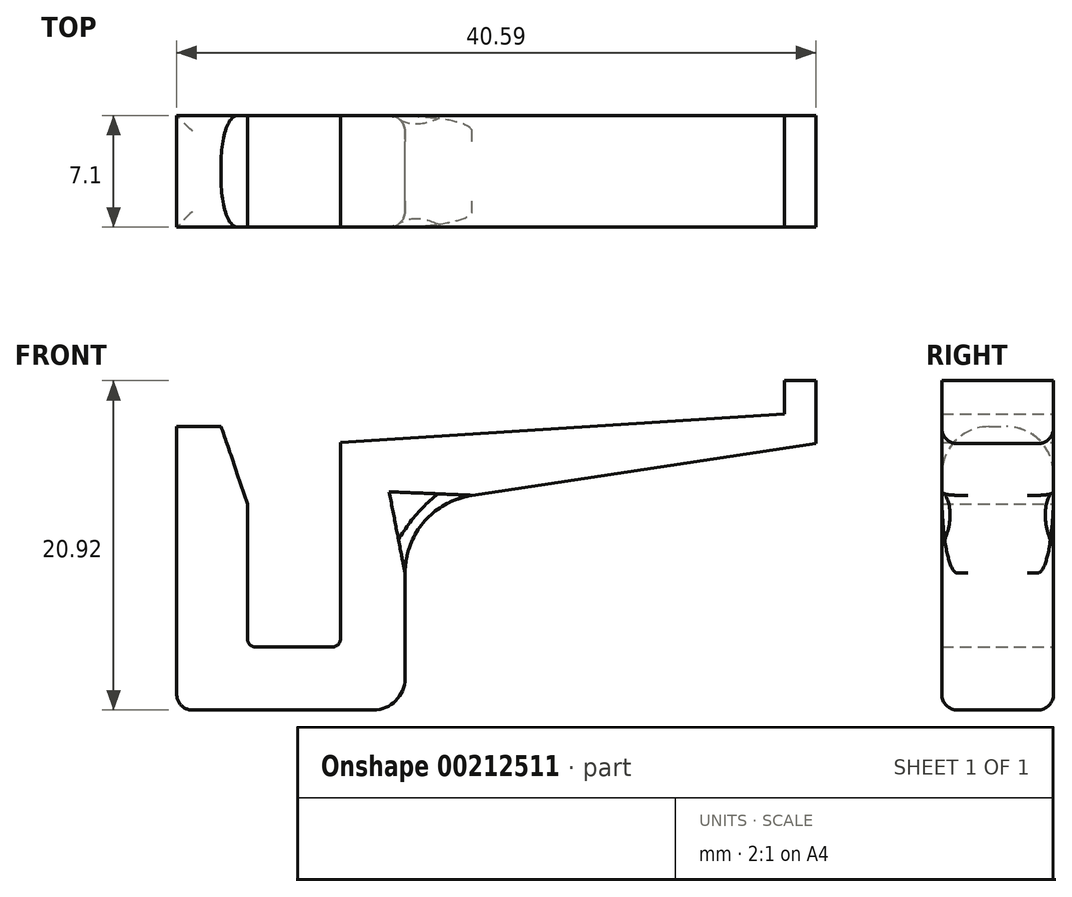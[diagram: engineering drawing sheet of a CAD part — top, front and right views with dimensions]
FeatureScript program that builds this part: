
annotation { "Feature Type Name" : "Feature", "Feature Type Description" : "" }
export const myFeature = defineFeature(function(context is Context, id is Id, definition is map)
    precondition{}
    {
        {
            var Q0;
            Q0=qCreatedBy(makeId("Front.planeOp"),FACE);
            var sketch = newSketch(context, id + "F0", { "sketchPlane" : qUnion([Q0])});
            skLineSegment(sketch, "E0", {"start": v(4.69, 3.9) * mm, "end": v(4.69, 12.98) * mm});
            skLineSegment(sketch, "E1", {"start": v(0.19, 12.9) * mm, "end": v(0.19, -0.1) * mm});
            skLineSegment(sketch, "E2", {"start": v(0.19, -0.1) * mm, "end": v(14.69, -0.1) * mm});
            skLineSegment(sketch, "E3", {"start": v(14.69, -0.1) * mm, "end": v(14.69, 8.9) * mm});
            skLineSegment(sketch, "E4", {"start": v(10.59, 12.9) * mm, "end": v(10.59, 3.9) * mm});
            skLineSegment(sketch, "E5", {"start": v(10.59, 3.9) * mm, "end": v(4.69, 3.9) * mm});
            skLineSegment(sketch, "E6", {"start": v(1.34, 17.9) * mm, "end": v(3.01, 17.9) * mm});
            skLineSegment(sketch, "E7", {"start": v(0.19, 12.9) * mm, "end": v(0.19, 17.9) * mm});
            skLineSegment(sketch, "E8", {"start": v(1.34, 17.9) * mm, "end": v(0.19, 17.9) * mm});
            skLineSegment(sketch, "E9", {"start": v(10.59, 12.9) * mm, "end": v(10.59, 16.9) * mm});
            skLineSegment(sketch, "E10", {"start": v(10.59, 16.9) * mm, "end": v(38.78, 18.7) * mm});
            skLineSegment(sketch, "E11", {"start": v(40.78, 18.82) * mm, "end": v(40.78, 16.82) * mm});
            skLineSegment(sketch, "E12", {"start": v(14.69, 8.9) * mm, "end": v(14.69, 12.9) * mm});
            skLineSegment(sketch, "E13", {"start": v(40.78, 16.82) * mm, "end": v(14.69, 12.9) * mm});
            skLineSegment(sketch, "E14", {"start": v(40.78, 18.82) * mm, "end": v(40.78, 20.82) * mm});
            skLineSegment(sketch, "E15", {"start": v(40.78, 20.82) * mm, "end": v(38.78, 20.82) * mm});
            skLineSegment(sketch, "E16", {"start": v(38.78, 20.82) * mm, "end": v(38.78, 18.7) * mm});
            skLineSegment(sketch, "E17", {"start": v(3.01, 17.9) * mm, "end": v(4.69, 12.98) * mm});
            skPoint(sketch, "E18.orphan", {"position": v(4.69, 17.9) * mm});
            skSolve(sketch);
        }
        {
            var Q0;
            Q0=makeQuery(id+"F0.imprint","IMPRINT",FACE,{"disambiguationData":[TD([[makeQuery(id+"F0.imprint","IMPRINT",EDGE,{"derivedFrom":sQuery(id+"F0.wireOp",EDGE,"E0")}),1.0]])]});
            extrude(context, id + "F1", {"entities" : qUnion([Q0]), "endBound" : BoundingType.SYMMETRIC, "depth" : 7.1 * mm});
        }
        {
            var Q0;
            Q0=makeQuery(id+"F1.opExtrude","CAP_EDGE",EDGE,{"disambiguationData":[OSD([sQuery(id+"F0.wireOp",EDGE,"FIeobUB5-AtsX-6hmR-oWOE-ariMEtalVAF4")])],"isStart":false});
            var Q1;
            Q1=makeQuery(id+"F1.opExtrude","SWEPT_EDGE",EDGE,{"disambiguationData":[OSD([sQuery(id+"F0.wireOp",EDGE,"5An7Op3Y-UuDj-N7TT-U8in-DWvZWZOJ67oY"),sQuery(id+"F0.wireOp",EDGE,"FIeobUB5-AtsX-6hmR-oWOE-ariMEtalVAF4")])]});
            var Q2;
            Q2=makeQuery(id+"F1.opExtrude","CAP_EDGE",EDGE,{"disambiguationData":[OSD([sQuery(id+"F0.wireOp",EDGE,"FIeobUB5-AtsX-6hmR-oWOE-ariMEtalVAF4")])],"isStart":true});
            var Q3;
            Q3=makeQuery(id+"F1.opExtrude","SWEPT_EDGE",EDGE,{"disambiguationData":[OSD([sQuery(id+"F0.wireOp",EDGE,"5An7Op3Y-UuDj-N7TT-U8in-DWvZWZOJ67oY"),sQuery(id+"F0.wireOp",EDGE,"z2avqr7E-bqeD-pCF3-mnLU-iVtxecrn7GOb")])]});
            var Q4;
            Q4=makeQuery(id+"F1.opExtrude","CAP_EDGE",EDGE,{"disambiguationData":[OSD([sQuery(id+"F0.wireOp",EDGE,"z2avqr7E-bqeD-pCF3-mnLU-iVtxecrn7GOb")])],"isStart":false});
            var Q5;
            Q5=makeQuery(id+"F1.opExtrude","CAP_EDGE",EDGE,{"disambiguationData":[OSD([sQuery(id+"F0.wireOp",EDGE,"z2avqr7E-bqeD-pCF3-mnLU-iVtxecrn7GOb")])],"isStart":true});
            var Q6;
            Q6=makeQuery(id+"F1.opExtrude","SWEPT_EDGE",EDGE,{"disambiguationData":[OSD([sQuery(id+"F0.wireOp",EDGE,"E0"),sQuery(id+"F0.wireOp",EDGE,"E5")])]});
            var Q7;
            Q7=makeQuery(id+"F1.opExtrude","SWEPT_EDGE",EDGE,{"disambiguationData":[OSD([sQuery(id+"F0.wireOp",EDGE,"E4"),sQuery(id+"F0.wireOp",EDGE,"E5")])]});
            fillet(context, id + "F2", {"entities" : qUnion([Q0, Q1, Q2, Q3, Q4, Q5, Q6, Q7]), "radius" : 0.5 * mm, "tangentPropagation" : true, "allowEdgeOverflow" : false});
        }
        {
            var Q0;
            Q0=makeQuery(id+"F1.opExtrude","SWEPT_EDGE",EDGE,{"disambiguationData":[OSD([sQuery(id+"F0.wireOp",EDGE,"E3"),sQuery(id+"F0.wireOp",EDGE,"z2avqr7E-bqeD-pCF3-mnLU-iVtxecrn7GOb")])]});
            fillet(context, id + "F3", {"entities" : qUnion([Q0]), "radius" : 2 * mm, "tangentPropagation" : true, "allowEdgeOverflow" : false});
        }
        {
            var Q0;
            Q0=makeQuery(id+"F1.opExtrude","SWEPT_EDGE",EDGE,{"disambiguationData":[OSD([sQuery(id+"F0.wireOp",EDGE,"FIeobUB5-AtsX-6hmR-oWOE-ariMEtalVAF4"),sQuery(id+"F0.wireOp",EDGE,"E4")])]});
            var Q1;
            Q1=makeQuery(id+"F1.opExtrude","CAP_EDGE",EDGE,{"disambiguationData":[OSD([sQuery(id+"F0.wireOp",EDGE,"E2")])],"isStart":false});
            var Q2;
            Q2=makeQuery(id+"F1.opExtrude","CAP_EDGE",EDGE,{"disambiguationData":[OSD([sQuery(id+"F0.wireOp",EDGE,"E2")])],"isStart":true});
            var Q3;
            Q3=makeQuery(id+"F1.opExtrude","CAP_EDGE",EDGE,{"disambiguationData":[OSD([sQuery(id+"F0.wireOp",EDGE,"E13")])],"isStart":false});
            var Q4;
            Q4=makeQuery(id+"F1.opExtrude","CAP_EDGE",EDGE,{"disambiguationData":[OSD([sQuery(id+"F0.wireOp",EDGE,"E13")])],"isStart":true});
            var Q5;
            Q5=makeQuery(id+"F1.opExtrude","SWEPT_EDGE",EDGE,{"disambiguationData":[OSD([sQuery(id+"F0.wireOp",EDGE,"E1"),sQuery(id+"F0.wireOp",EDGE,"E2")])]});
            fillet(context, id + "F4", {"entities" : qUnion([Q0, Q1, Q2, Q3, Q4, Q5]), "radius" : 1 * mm, "tangentPropagation" : true, "allowEdgeOverflow" : false});
        }
        {
            var Q0;
            Q0=makeQuery(id+"F1.opExtrude","CAP_EDGE",EDGE,{"disambiguationData":[OSD([sQuery(id+"F0.wireOp",EDGE,"E6"),sQuery(id+"F0.wireOp",EDGE,"E8")])],"isStart":true});
            var Q1;
            Q1=makeQuery(id+"F1.opExtrude","CAP_EDGE",EDGE,{"disambiguationData":[OSD([sQuery(id+"F0.wireOp",EDGE,"E6"),sQuery(id+"F0.wireOp",EDGE,"E8")])],"isStart":false});
            fillet(context, id + "F5", {"entities" : qUnion([Q0, Q1]), "radius" : 3 * mm, "tangentPropagation" : true, "allowEdgeOverflow" : false});
        }
        {
            var Q0;
            Q0=makeQuery(id+"F1.opExtrude","SWEPT_EDGE",EDGE,{"disambiguationData":[OSD([sQuery(id+"F0.wireOp",EDGE,"E12"),sQuery(id+"F0.wireOp",EDGE,"E13")])]});
            fillet(context, id + "F6", {"entities" : qUnion([Q0]), "radius" : 5 * mm, "tangentPropagation" : true, "allowEdgeOverflow" : false});
        }
    });
